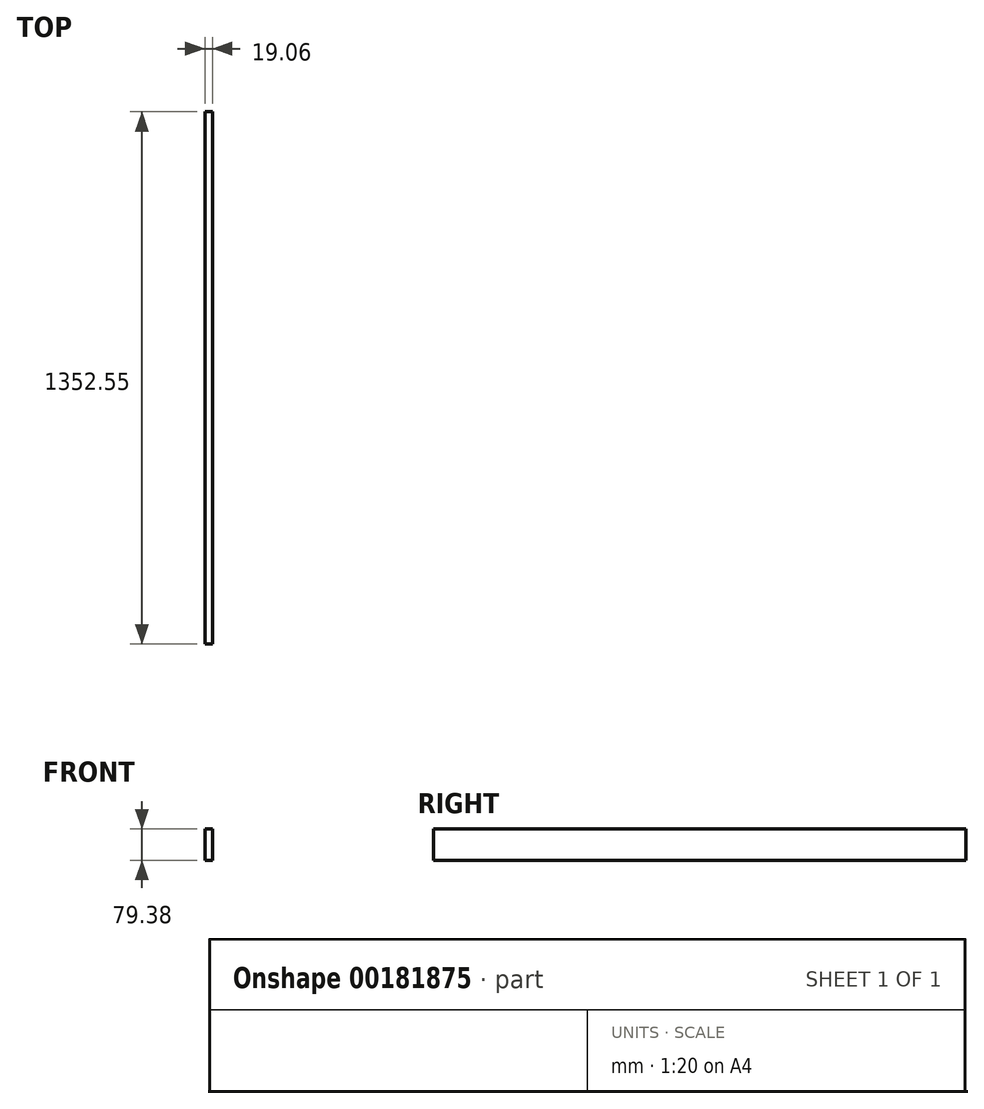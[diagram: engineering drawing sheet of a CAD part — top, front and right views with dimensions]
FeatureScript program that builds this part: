
annotation { "Feature Type Name" : "Feature", "Feature Type Description" : "" }
export const myFeature = defineFeature(function(context is Context, id is Id, definition is map)
    precondition{}
    {
        {
            var Q0;
            Q0=qCreatedBy(makeId("Front.planeOp"),FACE);
            var sketch = newSketch(context, id + "F0", { "sketchPlane" : qUnion([Q0])});
            skLineSegment(sketch, "E0.bottom", {"start": v(9.52, -39.69) * mm, "end": v(-9.53, -39.69) * mm});
            skLineSegment(sketch, "E0.top", {"start": v(9.53, 39.69) * mm, "end": v(-9.52, 39.69) * mm});
            skLineSegment(sketch, "E0.left", {"start": v(9.52, -39.69) * mm, "end": v(9.53, 39.69) * mm});
            skLineSegment(sketch, "E0.right", {"start": v(-9.53, -39.69) * mm, "end": v(-9.52, 39.69) * mm});
            skPoint(sketch, "E0.middle", {"position": v(0, 0) * mm});
            skSolve(sketch);
        }
        {
            var Q0;
            Q0=makeQuery(id+"F0.imprint","IMPRINT",FACE,{"disambiguationData":[TD([[makeQuery(id+"F0.imprint","IMPRINT",EDGE,{"derivedFrom":sQuery(id+"F0.wireOp",EDGE,"E0.bottom")}),-1.0]])]});
            extrude(context, id + "F1", {"entities" : qUnion([Q0]), "depth" : 1352.55 * mm});
        }
    });
